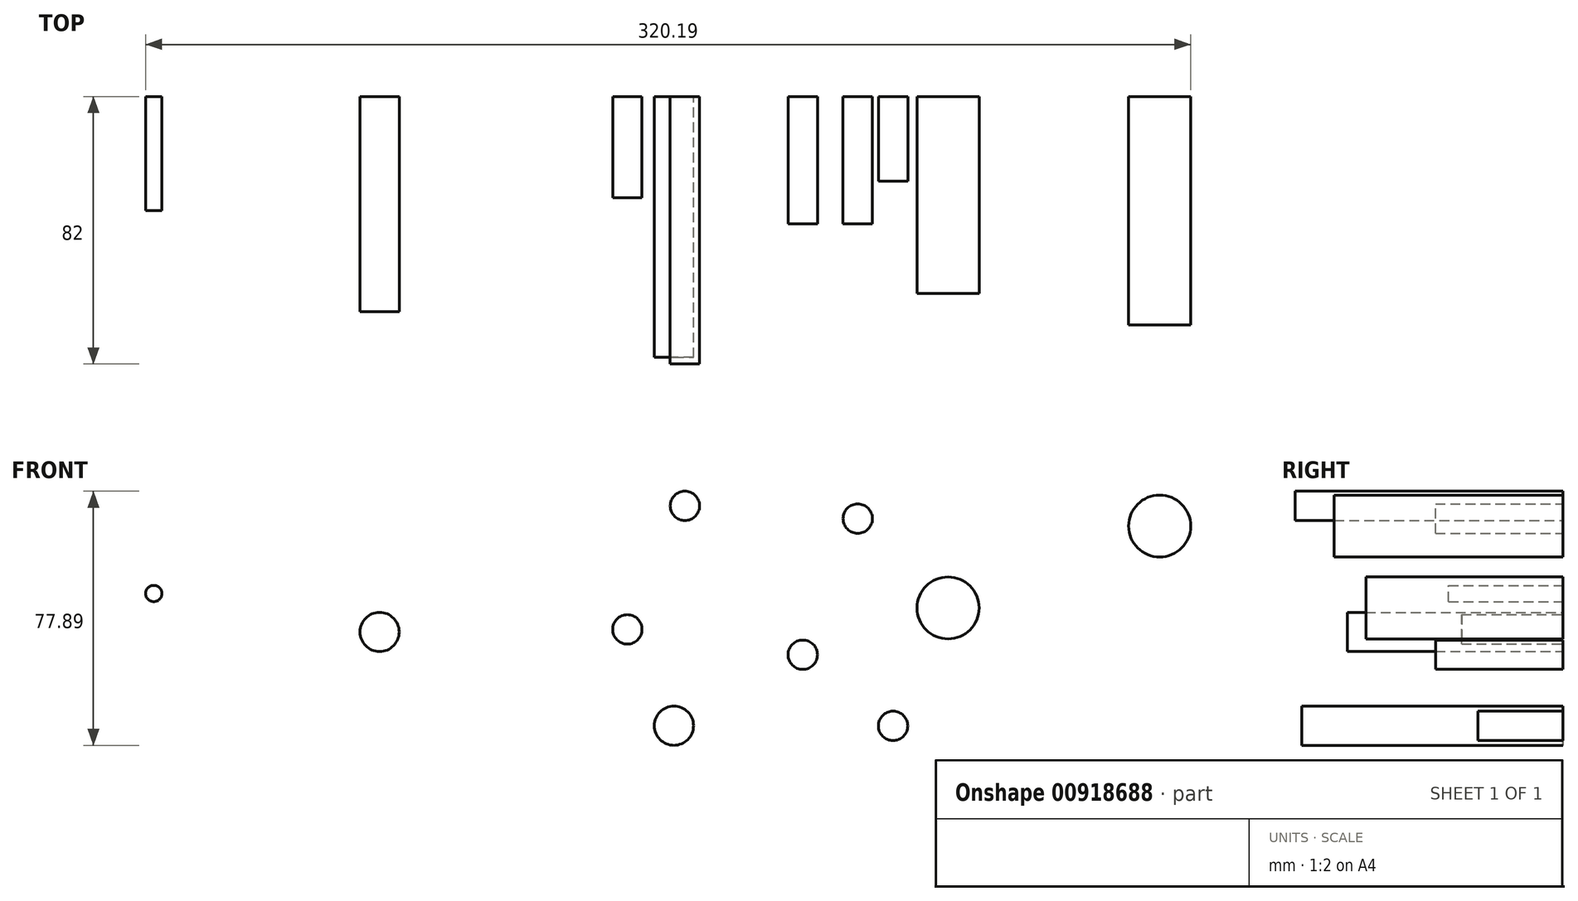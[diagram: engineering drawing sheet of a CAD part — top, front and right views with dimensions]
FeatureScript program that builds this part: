
annotation { "Feature Type Name" : "Feature", "Feature Type Description" : "" }
export const myFeature = defineFeature(function(context is Context, id is Id, definition is map)
    precondition{}
    {
        {
            var Q0;
            Q0=qCreatedBy(makeId("Front.planeOp"),FACE);
            var sketch = newSketch(context, id + "F0", { "sketchPlane" : qUnion([Q0])});
            skCircle(sketch, "E0", {"center": v(0, 0) * mm, "radius": 4.5 * mm});
            skSolve(sketch);
        }
        {
            var Q0;
            Q0 = qSketchRegion(id + "F0", true);
            extrude(context, id + "F1", {"entities" : qUnion([Q0]), "depth" : 39 * mm, "offsetDistance" : 25 * mm});
        }
        {
            var Q0;
            Q0=qCreatedBy(makeId("Front.planeOp"),FACE);
            var sketch = newSketch(context, id + "F2", { "sketchPlane" : qUnion([Q0])});
            skCircle(sketch, "E1", {"center": v(-36.1, 45.63) * mm, "radius": 4.5 * mm});
            skSolve(sketch);
        }
        {
            var Q0;
            Q0=makeQuery(id+"F2.imprint","IMPRINT",FACE,{"disambiguationData":[TD([[makeQuery(id+"F2.imprint","IMPRINT",EDGE,{"derivedFrom":sQuery(id+"F2.wireOp",EDGE,"E1")}),1.0]])]});
            extrude(context, id + "F3", {"entities" : qUnion([Q0]), "depth" : 82 * mm, "offsetDistance" : 25 * mm});
        }
        {
            var Q0;
            Q0=qCreatedBy(makeId("Front.planeOp"),FACE);
            var sketch = newSketch(context, id + "F4", { "sketchPlane" : qUnion([Q0])});
            skCircle(sketch, "E2", {"center": v(44.51, 14.34) * mm, "radius": 9.5 * mm});
            skSolve(sketch);
        }
        {
            var Q0;
            Q0=makeQuery(id+"F4.imprint","IMPRINT",FACE,{"disambiguationData":[TD([[makeQuery(id+"F4.imprint","IMPRINT",EDGE,{"derivedFrom":sQuery(id+"F4.wireOp",EDGE,"E2")}),1.0]])]});
            extrude(context, id + "F5", {"entities" : qUnion([Q0]), "depth" : 60.33 * mm, "offsetDistance" : 25 * mm});
        }
        {
            var Q0;
            Q0=qCreatedBy(makeId("Front.planeOp"),FACE);
            var sketch = newSketch(context, id + "F6", { "sketchPlane" : qUnion([Q0])});
            skCircle(sketch, "E3", {"center": v(-53.74, 7.76) * mm, "radius": 4.5 * mm});
            skSolve(sketch);
        }
        {
            var Q0;
            Q0 = qSketchRegion(id + "F6", true);
            extrude(context, id + "F7", {"entities" : qUnion([Q0]), "depth" : 31 * mm, "offsetDistance" : 25 * mm});
        }
        {
            var Q0;
            Q0=qCreatedBy(makeId("Front.planeOp"),FACE);
            var sketch = newSketch(context, id + "F8", { "sketchPlane" : qUnion([Q0])});
            skCircle(sketch, "E4", {"center": v(-39.47, -21.76) * mm, "radius": 6 * mm});
            skSolve(sketch);
        }
        {
            var Q0;
            Q0=makeQuery(id+"F8.imprint","IMPRINT",FACE,{"disambiguationData":[TD([[makeQuery(id+"F8.imprint","IMPRINT",EDGE,{"derivedFrom":sQuery(id+"F8.wireOp",EDGE,"E4")}),1.0]])]});
            extrude(context, id + "F9", {"entities" : qUnion([Q0]), "depth" : 80 * mm, "offsetDistance" : 25 * mm});
        }
        {
            var Q0;
            Q0=qCreatedBy(makeId("Front.planeOp"),FACE);
            var sketch = newSketch(context, id + "F10", { "sketchPlane" : qUnion([Q0])});
            skCircle(sketch, "E5", {"center": v(27.67, -21.82) * mm, "radius": 4.5 * mm});
            skSolve(sketch);
        }
        {
            var Q0;
            Q0=makeQuery(id+"F10.imprint","IMPRINT",FACE,{"disambiguationData":[TD([[makeQuery(id+"F10.imprint","IMPRINT",EDGE,{"derivedFrom":sQuery(id+"F10.wireOp",EDGE,"E5")}),1.0]])]});
            extrude(context, id + "F11", {"entities" : qUnion([Q0]), "depth" : 26 * mm, "offsetDistance" : 25 * mm});
        }
        {
            var Q0;
            Q0=qCreatedBy(makeId("Front.planeOp"),FACE);
            var sketch = newSketch(context, id + "F12", { "sketchPlane" : qUnion([Q0])});
            skCircle(sketch, "E6", {"center": v(16.84, 41.73) * mm, "radius": 4.5 * mm});
            skSolve(sketch);
        }
        {
            var Q0;
            Q0=makeQuery(id+"F12.imprint","IMPRINT",FACE,{"disambiguationData":[TD([[makeQuery(id+"F12.imprint","IMPRINT",EDGE,{"derivedFrom":sQuery(id+"F12.wireOp",EDGE,"E6")}),1.0]])]});
            extrude(context, id + "F13", {"entities" : qUnion([Q0]), "depth" : 39 * mm, "offsetDistance" : 25 * mm});
        }
        {
            var Q0;
            Q0=qCreatedBy(makeId("Front.planeOp"),FACE);
            var sketch = newSketch(context, id + "F14", { "sketchPlane" : qUnion([Q0])});
            skCircle(sketch, "E7", {"center": v(109.35, 39.44) * mm, "radius": 9.5 * mm});
            skSolve(sketch);
        }
        {
            var Q0;
            Q0=makeQuery(id+"F14.imprint","IMPRINT",FACE,{"disambiguationData":[TD([[makeQuery(id+"F14.imprint","IMPRINT",EDGE,{"derivedFrom":sQuery(id+"F14.wireOp",EDGE,"E7")}),1.0]])]});
            extrude(context, id + "F15", {"entities" : qUnion([Q0]), "depth" : 70 * mm, "offsetDistance" : 25 * mm});
        }
        {
            var Q0;
            Q0=qCreatedBy(makeId("Front.planeOp"),FACE);
            var sketch = newSketch(context, id + "F16", { "sketchPlane" : qUnion([Q0])});
            skCircle(sketch, "E8", {"center": v(-129.66, 6.98) * mm, "radius": 6 * mm});
            skSolve(sketch);
        }
        {
            var Q0;
            Q0 = qSketchRegion(id + "F16", true);
            extrude(context, id + "F17", {"entities" : qUnion([Q0]), "depth" : 66 * mm, "offsetDistance" : 25 * mm});
        }
        {
            var Q0;
            Q0=qCreatedBy(makeId("Front.planeOp"),FACE);
            var sketch = newSketch(context, id + "F18", { "sketchPlane" : qUnion([Q0])});
            skCircle(sketch, "E9", {"center": v(-198.84, 18.77) * mm, "radius": 2.5 * mm});
            skSolve(sketch);
        }
        {
            var Q0;
            Q0 = qSketchRegion(id + "F18", true);
            extrude(context, id + "F19", {"entities" : qUnion([Q0]), "depth" : 35 * mm, "offsetDistance" : 25 * mm});
        }
    });
